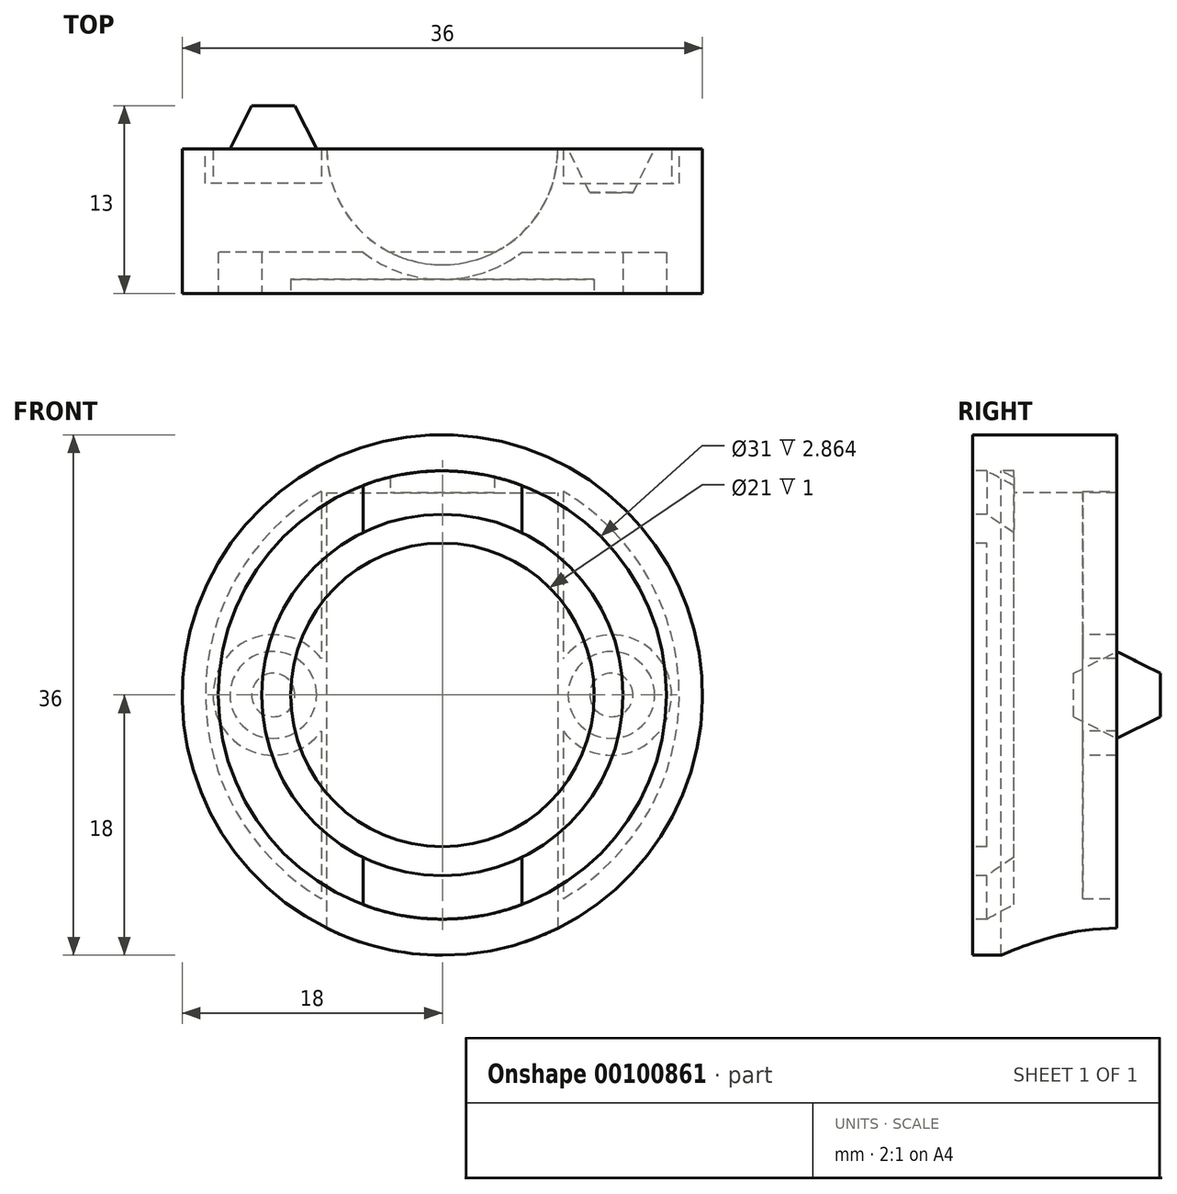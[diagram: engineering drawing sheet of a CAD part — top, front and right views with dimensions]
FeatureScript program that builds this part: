
annotation { "Feature Type Name" : "Feature", "Feature Type Description" : "" }
export const myFeature = defineFeature(function(context is Context, id is Id, definition is map)
    precondition{}
    {
        {
            var Q0;
            Q0=qCreatedBy(makeId("Front.planeOp"),FACE);
            var sketch = newSketch(context, id + "F0", { "sketchPlane" : qUnion([Q0])});
            skCircle(sketch, "E0", {"center": v(0, 0) * mm, "radius": 18 * mm});
            skSolve(sketch);
        }
        {
            var Q0;
            Q0 = qSketchRegion(id + "F0", true);
            extrude(context, id + "F1", {"entities" : qUnion([Q0]), "depth" : 10 * mm});
        }
        {
            var Q0;
            Q0=makeQuery(id+"F1.opExtrude","CAP_FACE",FACE,{"disambiguationData":[OSD([sQuery(id+"F0.wireOp",EDGE,"E0")])],"isStart":false});
            var sketch = newSketch(context, id + "F2", { "sketchPlane" : qUnion([Q0])});
            skCircle(sketch, "E1", {"center": v(0, 0) * mm, "radius": 10.5 * mm});
            skSolve(sketch);
        }
        {
            var Q0;
            Q0 = qSketchRegion(id + "F2", true);
            extrude(context, id + "F3", {"entities" : qUnion([Q0]), "operationType" : NewBodyOperationType.REMOVE, "oppositeDirection" : true, "depth" : 1 * mm});
        }
        {
            var Q0;
            Q0=makeQuery(id+"F1.opExtrude","CAP_FACE",FACE,{"disambiguationData":[OSD([sQuery(id+"F0.wireOp",EDGE,"E0")])],"isStart":false});
            var sketch = newSketch(context, id + "F4", { "sketchPlane" : qUnion([Q0])});
            skCircle(sketch, "E2", {"center": v(0, 0) * mm, "radius": 12.5 * mm});
            skCircle(sketch, "E3", {"center": v(0, 0) * mm, "radius": 15.5 * mm});
            skSolve(sketch);
        }
        {
            var Q0;
            Q0 = qSketchRegion(id + "F4", true);
            extrude(context, id + "F5", {"entities" : qUnion([Q0]), "operationType" : NewBodyOperationType.REMOVE, "oppositeDirection" : true, "depth" : 2.86 * mm});
        }
        {
            var Q0;
            Q0=makeQuery(id+"F1.opExtrude","CAP_FACE",FACE,{"disambiguationData":[OSD([sQuery(id+"F0.wireOp",EDGE,"E0")])],"isStart":true});
            var sketch = newSketch(context, id + "F6", { "sketchPlane" : qUnion([Q0])});
            skArc(sketch, "E4", {"start": v(-8.37, 14.09) * mm, "mid": v(-16.39, 0) * mm, "end": v(-8.37, -14.09) * mm});
            skLineSegment(sketch, "E5", {"start": v(-8.37, 14.09) * mm, "end": v(-8.37, -14.09) * mm});
            skLineSegment(sketch, "E6.MirrorCS", {"start": v(8.37, 14.09) * mm, "end": v(8.37, -14.09) * mm});
            skArc(sketch, "E7.trimOffspring", {"start": v(8.37, -14.09) * mm, "mid": v(16.39, 0) * mm, "end": v(8.37, 14.09) * mm});
            skSolve(sketch);
        }
        {
            var Q0;
            Q0 = qSketchRegion(id + "F6", true);
            extrude(context, id + "F7", {"entities" : qUnion([Q0]), "operationType" : NewBodyOperationType.REMOVE, "oppositeDirection" : true, "depth" : 2.38 * mm});
        }
        {
            var Q0;
            Q0=makeQuery(id+"F7.boolean.opBoolean","COPY",FACE,{"derivedFrom":makeQuery(id+"F7.opExtrude","CAP_FACE",FACE,{"disambiguationData":[OSD([sQuery(id+"F6.wireOp",EDGE,"E4"),sQuery(id+"F6.wireOp",EDGE,"E5")])],"isStart":false})});
            var sketch = newSketch(context, id + "F8", { "sketchPlane" : qUnion([Q0])});
            skCircle(sketch, "E8", {"center": v(-11.7, 0) * mm, "radius": 4.17 * mm});
            skCircle(sketch, "E9.MirrorC", {"center": v(11.7, 0) * mm, "radius": 4.17 * mm});
            skSolve(sketch);
        }
        {
            var Q0;
            Q0 = qSketchRegion(id + "F8", true);
            var Q1;
            Q1=makeQuery(id+"F1.opExtrude","CAP_FACE",FACE,{"disambiguationData":[OSD([sQuery(id+"F0.wireOp",EDGE,"E0")])],"isStart":true});
            extrude(context, id + "F9", {"entities" : qUnion([Q0]), "operationType" : NewBodyOperationType.ADD, "endBound" : BoundingType.UP_TO_SURFACE, "endBoundEntityFace" : qUnion([Q1]), "depth" : 2.42 * mm});
        }
        {
            var Q0;
            Q0=qCreatedBy(makeId("Top.planeOp"),FACE);
            var sketch = newSketch(context, id + "F10", { "sketchPlane" : qUnion([Q0])});
            skArc(sketch, "E10", {"start": v(-8, 0) * mm, "mid": v(0, -8) * mm, "end": v(8, 0) * mm});
            skLineSegment(sketch, "E11", {"start": v(-8, 0) * mm, "end": v(8, 0) * mm});
            skSolve(sketch);
        }
        {
            var Q0;
            Q0=qCreatedBy(makeId("Top.planeOp"),FACE);
            var sketch = newSketch(context, id + "F11", { "sketchPlane" : qUnion([Q0])});
            skLineSegment(sketch, "E12", {"start": v(-11.7, 3.11) * mm, "end": v(-11.7, -5.52) * mm, "construction": true});
            skLineSegment(sketch, "E13", {"start": v(-11.7, 0) * mm, "end": v(-8.7, 0) * mm});
            skLineSegment(sketch, "E14", {"start": v(-8.7, 0) * mm, "end": v(-10.2, 3) * mm});
            skLineSegment(sketch, "E15", {"start": v(-10.2, 3) * mm, "end": v(-11.7, 3) * mm});
            skLineSegment(sketch, "E16", {"start": v(-11.7, 3) * mm, "end": v(-11.7, 0) * mm});
            skSolve(sketch);
        }
        {
            var Q0;
            Q0 = qSketchRegion(id + "F11", true);
            var Q1;
            Q1=sQuery(id+"F11.wireOp",EDGE,"E12");
            revolve(context, id + "F12", {"operationType" : NewBodyOperationType.ADD, "entities" : qUnion([Q0]), "axis" : qUnion([Q1]), "revolveType" : RevolveType.FULL});
        }
        {
            var Q0;
            Q0=qCreatedBy(makeId("Top.planeOp"),FACE);
            var sketch = newSketch(context, id + "F13", { "sketchPlane" : qUnion([Q0])});
            skLineSegment(sketch, "E17", {"start": v(11.7, 3.78) * mm, "end": v(11.7, -11.62) * mm, "construction": true});
            skLineSegment(sketch, "E18", {"start": v(11.7, 0) * mm, "end": v(14.7, 0) * mm});
            skLineSegment(sketch, "E19", {"start": v(14.7, 0) * mm, "end": v(13.2, -3) * mm});
            skLineSegment(sketch, "E20", {"start": v(13.2, -3) * mm, "end": v(11.7, -3) * mm});
            skLineSegment(sketch, "E21", {"start": v(11.7, -3) * mm, "end": v(11.7, 0) * mm});
            skSolve(sketch);
        }
        {
            var Q0;
            Q0 = qSketchRegion(id + "F13", true);
            var Q1;
            Q1=sQuery(id+"F13.wireOp",EDGE,"E17");
            revolve(context, id + "F14", {"operationType" : NewBodyOperationType.REMOVE, "entities" : qUnion([Q0]), "axis" : qUnion([Q1]), "revolveType" : RevolveType.FULL, "oppositeDirection" : true});
        }
        {
            var Q0;
            Q0 = qSketchRegion(id + "F10", true);
            extrude(context, id + "F15", {"entities" : qUnion([Q0]), "operationType" : NewBodyOperationType.REMOVE, "endBound" : BoundingType.THROUGH_ALL, "oppositeDirection" : true, "depth" : 25.4 * mm, "hasSecondDirection" : true, "secondDirectionOppositeDirection" : false, "secondDirectionDepth" : 13.97 * mm});
        }
        {
            var Q0;
            Q0=qCreatedBy(makeId("Top.planeOp"),FACE);
            var sketch = newSketch(context, id + "F16", { "sketchPlane" : qUnion([Q0])});
            skArc(sketch, "E22", {"start": v(-6.5, -6.24) * mm, "mid": v(-0.04, -9) * mm, "end": v(6.43, -6.3) * mm});
            skLineSegment(sketch, "E23", {"start": v(-9, 0) * mm, "end": v(9, 0) * mm});
            skArc(sketch, "E24", {"start": v(-5, -6.24) * mm, "mid": v(-0.05, -8) * mm, "end": v(4.92, -6.3) * mm});
            skLineSegment(sketch, "E25", {"start": v(-6.5, -6.24) * mm, "end": v(-5, -6.24) * mm});
            skLineSegment(sketch, "E26", {"start": v(4.92, -6.3) * mm, "end": v(6.43, -6.3) * mm});
            skSolve(sketch);
        }
        {
            var Q0;
            Q0 = qSketchRegion(id + "F16", true);
            var Q1;
            Q1=makeQuery(id+"F5.boolean.opBoolean","COPY",FACE,{"derivedFrom":makeQuery(id+"F5.opExtrude","SWEPT_FACE",FACE,{"disambiguationData":[OSD([sQuery(id+"F4.wireOp",EDGE,"E3")])]})});
            var Q2;
            Q2=makeQuery(id+"F5.boolean.opBoolean","COPY",FACE,{"derivedFrom":makeQuery(id+"F5.opExtrude","SWEPT_FACE",FACE,{"disambiguationData":[OSD([sQuery(id+"F4.wireOp",EDGE,"E2")])]})});
            extrude(context, id + "F17", {"entities" : qUnion([Q0]), "operationType" : NewBodyOperationType.ADD, "endBound" : BoundingType.UP_TO_SURFACE, "endBoundEntityFace" : qUnion([Q1]), "depth" : 13.97 * mm, "hasSecondDirection" : true, "secondDirectionBound" : SecondDirectionBoundingType.UP_TO_SURFACE, "secondDirectionOppositeDirection" : false, "secondDirectionBoundEntityFace" : qUnion([Q2]), "secondDirectionDepth" : 25.4 * mm});
        }
        {
            var Q0;
            Q0 = qSketchRegion(id + "F16", true);
            var Q1;
            {var subQ0=sQuery(id+"F4.wireOp",EDGE,"E3");Q1=makeQuery(id+"F17.boolean.opBoolean","SPLIT",FACE,{"disambiguationData":[TD([makeQuery(id+"F1.opExtrude","CAP_FACE",FACE,{"disambiguationData":[OSD([sQuery(id+"F0.wireOp",EDGE,"E0")])],"isStart":false}),makeQuery(id+"F5.boolean.opBoolean","COPY",FACE,{"derivedFrom":makeQuery(id+"F5.opExtrude","CAP_FACE",FACE,{"disambiguationData":[OSD([sQuery(id+"F4.wireOp",EDGE,"E2"),subQ0])],"isStart":false})}),makeQuery(id+"F15.boolean.opBoolean","COPY",FACE,{"derivedFrom":makeQuery(id+"F15.opExtrude","SWEPT_FACE",FACE,{"disambiguationData":[OSD([sQuery(id+"F10.wireOp",EDGE,"E10")])]})}),makeQuery(id+"F17.opExtrude","SWEPT_FACE",FACE,{"disambiguationData":[OSD([sQuery(id+"F16.wireOp",EDGE,"E22")])]}),makeQuery(id+"F17.opExtrude","SWEPT_FACE",FACE,{"disambiguationData":[OSD([sQuery(id+"F16.wireOp",EDGE,"E24")])]})])],"derivedFrom":makeQuery(id+"F5.boolean.opBoolean","COPY",FACE,{"derivedFrom":makeQuery(id+"F5.opExtrude","SWEPT_FACE",FACE,{"disambiguationData":[OSD([subQ0])]})})});}
            var Q2;
            Q2=makeQuery(id+"F5.boolean.opBoolean","COPY",FACE,{"derivedFrom":makeQuery(id+"F5.opExtrude","SWEPT_FACE",FACE,{"disambiguationData":[OSD([sQuery(id+"F4.wireOp",EDGE,"E2")])]})});
            extrude(context, id + "F18", {"entities" : qUnion([Q0]), "operationType" : NewBodyOperationType.ADD, "endBound" : BoundingType.UP_TO_SURFACE, "oppositeDirection" : true, "endBoundEntityFace" : qUnion([Q1]), "depth" : 25.4 * mm, "hasSecondDirection" : true, "secondDirectionBound" : SecondDirectionBoundingType.UP_TO_SURFACE, "secondDirectionOppositeDirection" : true, "secondDirectionBoundEntityFace" : qUnion([Q2]), "secondDirectionDepth" : 25.4 * mm});
        }
    });
